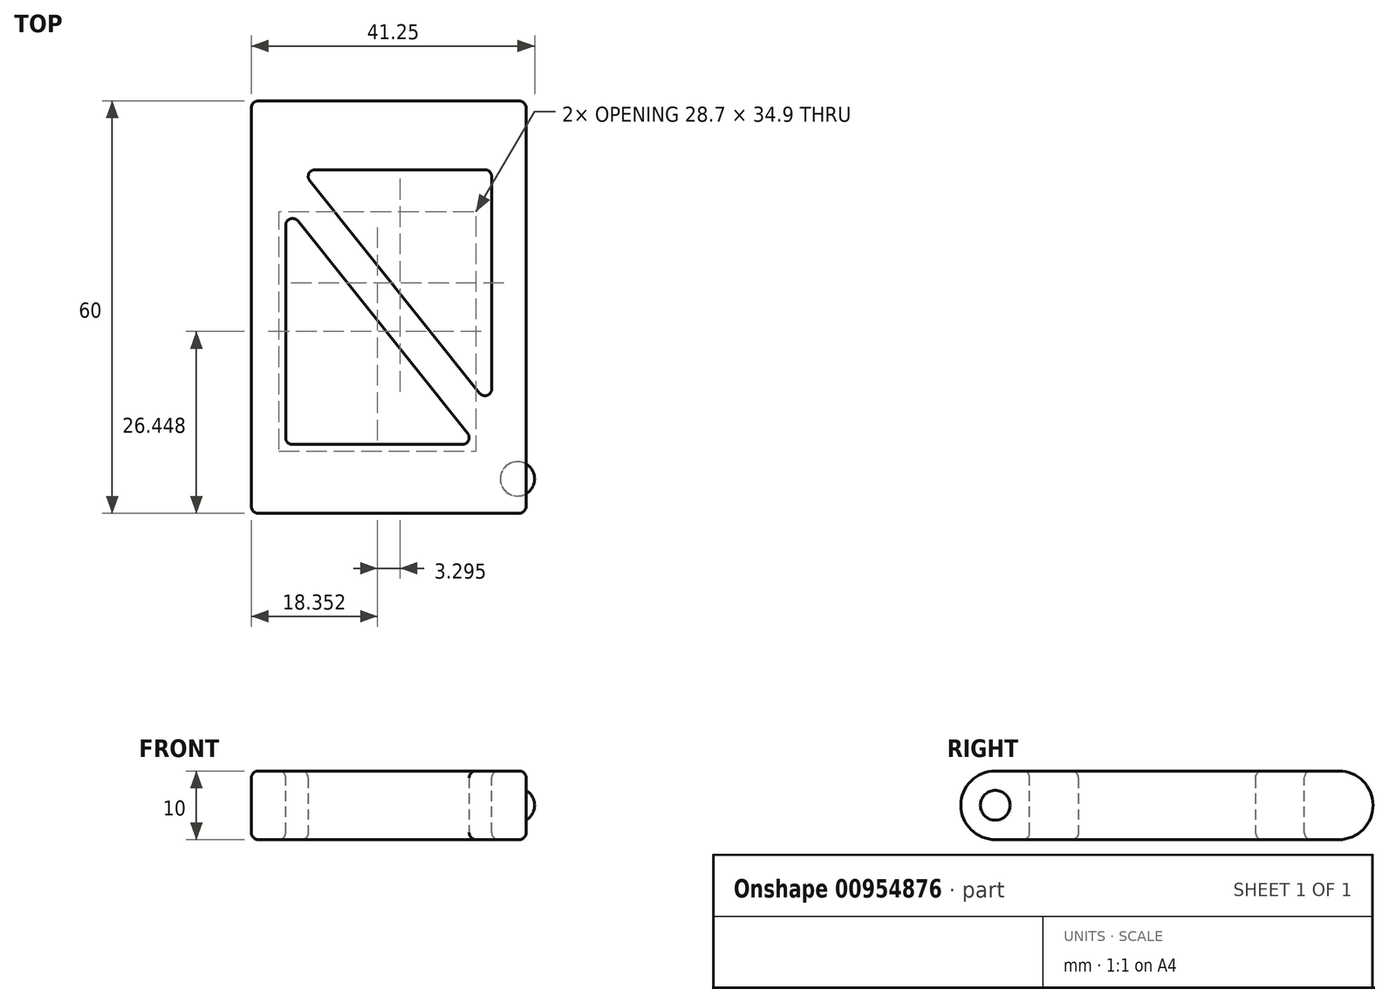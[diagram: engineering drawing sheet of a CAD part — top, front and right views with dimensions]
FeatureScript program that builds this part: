
annotation { "Feature Type Name" : "Feature", "Feature Type Description" : "" }
export const myFeature = defineFeature(function(context is Context, id is Id, definition is map)
    precondition{}
    {
        {
            var Q0;
            Q0=qCreatedBy(makeId("Top.planeOp"),FACE);
            var sketch = newSketch(context, id + "F0", { "sketchPlane" : qUnion([Q0])});
            skLineSegment(sketch, "E0.bottom", {"start": v(20, -30) * mm, "end": v(-20, -30) * mm});
            skLineSegment(sketch, "E0.top", {"start": v(20, 30) * mm, "end": v(-20, 30) * mm});
            skLineSegment(sketch, "E0.left", {"start": v(20, -30) * mm, "end": v(20, 30) * mm});
            skLineSegment(sketch, "E0.right", {"start": v(-20, -30) * mm, "end": v(-20, 30) * mm});
            skPoint(sketch, "E0.middle", {"position": v(0, 0) * mm});
            skSolve(sketch);
        }
        {
            var Q0;
            Q0=makeQuery(id+"F0.imprint","IMPRINT",FACE,{"disambiguationData":[TD([[makeQuery(id+"F0.imprint","IMPRINT",EDGE,{"derivedFrom":sQuery(id+"F0.wireOp",EDGE,"E0.bottom")}),-1.0]])]});
            extrude(context, id + "F1", {"entities" : qUnion([Q0]), "depth" : 5 * mm, "offsetDistance" : 25 * mm, "hasSecondDirection" : true, "secondDirectionOppositeDirection" : true, "secondDirectionDepth" : 5 * mm});
        }
        {
            var Q0;
            Q0=makeQuery(id+"F1.opExtrude","CAP_EDGE",EDGE,{"disambiguationData":[OSD([sQuery(id+"F0.wireOp",EDGE,"E0.bottom")])],"isStart":false});
            var Q1;
            Q1=makeQuery(id+"F1.opExtrude","CAP_EDGE",EDGE,{"disambiguationData":[OSD([sQuery(id+"F0.wireOp",EDGE,"E0.bottom")])],"isStart":true});
            var Q2;
            Q2=makeQuery(id+"F1.opExtrude","CAP_EDGE",EDGE,{"disambiguationData":[OSD([sQuery(id+"F0.wireOp",EDGE,"E0.top")])],"isStart":false});
            var Q3;
            Q3=makeQuery(id+"F1.opExtrude","CAP_EDGE",EDGE,{"disambiguationData":[OSD([sQuery(id+"F0.wireOp",EDGE,"E0.top")])],"isStart":true});
            fillet(context, id + "F2", {"entities" : qUnion([Q0, Q1, Q2, Q3]), "radius" : 5 * mm, "tangentPropagation" : true, "allowEdgeOverflow" : false});
        }
        {
            var Q0;
            Q0=qCreatedBy(makeId("Front.planeOp"),FACE);
            var Q1;
            {var subQ0=sQuery(id+"F0.wireOp",EDGE,"E0.left");var subQ1=sQuery(id+"F0.wireOp",EDGE,"E0.bottom");Q1=makeQuery(id+"F2.opFillet","BLEND_VERTEX",VERTEX,{"blendedFrom":[makeQuery(id+"F1.opExtrude","CAP_EDGE",EDGE,{"disambiguationData":[OSD([subQ1])],"isStart":false}),makeQuery(id+"F1.opExtrude","CAP_FACE",FACE,{"disambiguationData":[OSD([subQ1,sQuery(id+"F0.wireOp",EDGE,"E0.top"),subQ0,sQuery(id+"F0.wireOp",EDGE,"E0.right")])],"isStart":false}),makeQuery(id+"F1.opExtrude","SWEPT_FACE",FACE,{"disambiguationData":[OSD([subQ0])]})],"blendedInto":[makeQuery(id+"F1.opExtrude","CAP_FACE",FACE,{"disambiguationData":[OSD([subQ1,sQuery(id+"F0.wireOp",EDGE,"E0.top"),subQ0,sQuery(id+"F0.wireOp",EDGE,"E0.right")])],"isStart":false}),makeQuery(id+"F1.opExtrude","SWEPT_FACE",FACE,{"disambiguationData":[OSD([subQ0])]})]});}
            cPlane(context, id + "F3", {"entities" : qUnion([Q0, Q1]), "cplaneType" : CPlaneType.PLANE_POINT, "offset" : 25 * mm, "width" : 150 * mm, "height" : 150 * mm});
        }
        {
            var Q0;
            Q0=qCreatedBy(id+"F3.planeOp",FACE);
            var sketch = newSketch(context, id + "F4", { "sketchPlane" : qUnion([Q0])});
            skArc(sketch, "E1", {"start": v(18.75, -2.5) * mm, "mid": v(21.25, 0) * mm, "end": v(18.75, 2.5) * mm});
            skLineSegment(sketch, "E2", {"start": v(18.75, 2.5) * mm, "end": v(18.75, -2.5) * mm});
            skSolve(sketch);
        }
        {
            var Q0;
            Q0=makeQuery(id+"F4.imprint","IMPRINT",FACE,{"disambiguationData":[TD([[makeQuery(id+"F4.imprint","IMPRINT",EDGE,{"derivedFrom":sQuery(id+"F4.wireOp",EDGE,"E1")}),1.0]])]});
            var Q1;
            Q1=sQuery(id+"F4.wireOp",EDGE,"E2");
            revolve(context, id + "F5", {"operationType" : NewBodyOperationType.ADD, "surfaceOperationType" : NewSurfaceOperationType.NEW, "entities" : qUnion([Q0]), "axis" : qUnion([Q1]), "revolveType" : RevolveType.FULL});
        }
        {
            var Q0;
            Q0=qCreatedBy(makeId("Top.planeOp"),FACE);
            var sketch = newSketch(context, id + "F6", { "sketchPlane" : qUnion([Q0])});
            skLineSegment(sketch, "E3", {"start": v(-15, -20) * mm, "end": v(12.8, -20) * mm});
            skLineSegment(sketch, "E4", {"start": v(12.8, -20) * mm, "end": v(-15, 14.75) * mm});
            skLineSegment(sketch, "E5", {"start": v(-12.8, 20) * mm, "end": v(15, 20) * mm});
            skLineSegment(sketch, "E6", {"start": v(15, -14.75) * mm, "end": v(-12.8, 20) * mm});
            skLineSegment(sketch, "E7", {"start": v(-20, 25) * mm, "end": v(20, -25) * mm, "construction": true});
            skLineSegment(sketch, "E8", {"start": v(15, 20) * mm, "end": v(15, -14.75) * mm});
            skLineSegment(sketch, "E9", {"start": v(-15, 14.75) * mm, "end": v(-15, -20) * mm});
            skSolve(sketch);
        }
        {
            var Q0;
            Q0 = qSketchRegion(id + "F6", true);
            extrude(context, id + "F7", {"entities" : qUnion([Q0]), "operationType" : NewBodyOperationType.REMOVE, "endBound" : BoundingType.THROUGH_ALL, "oppositeDirection" : true, "depth" : 25 * mm, "offsetDistance" : 25 * mm, "hasSecondDirection" : true, "secondDirectionBound" : SecondDirectionBoundingType.THROUGH_ALL, "secondDirectionOppositeDirection" : false, "secondDirectionDepth" : 25 * mm});
        }
        {
            var Q0;
            Q0=makeQuery(id+"F1.opExtrude","CAP_EDGE",EDGE,{"disambiguationData":[OSD([sQuery(id+"F0.wireOp",EDGE,"E0.left")])],"isStart":false});
            var Q1;
            Q1=makeQuery(id+"F2.opFillet","BLEND_EDGE",EDGE,{"blendedFrom":[makeQuery(id+"F1.opExtrude","CAP_EDGE",EDGE,{"disambiguationData":[OSD([sQuery(id+"F0.wireOp",EDGE,"E0.top")])],"isStart":true}),makeQuery(id+"F1.opExtrude","SWEPT_FACE",FACE,{"disambiguationData":[OSD([sQuery(id+"F0.wireOp",EDGE,"E0.left")])]})],"blendedInto":[makeQuery(id+"F1.opExtrude","SWEPT_FACE",FACE,{"disambiguationData":[OSD([sQuery(id+"F0.wireOp",EDGE,"E0.left")])]})]});
            var Q2;
            Q2=makeQuery(id+"F2.opFillet","BLEND_EDGE",EDGE,{"blendedFrom":[makeQuery(id+"F1.opExtrude","CAP_EDGE",EDGE,{"disambiguationData":[OSD([sQuery(id+"F0.wireOp",EDGE,"E0.bottom")])],"isStart":true}),makeQuery(id+"F1.opExtrude","SWEPT_FACE",FACE,{"disambiguationData":[OSD([sQuery(id+"F0.wireOp",EDGE,"E0.left")])]})],"blendedInto":[makeQuery(id+"F1.opExtrude","SWEPT_FACE",FACE,{"disambiguationData":[OSD([sQuery(id+"F0.wireOp",EDGE,"E0.left")])]})]});
            var Q3;
            Q3=makeQuery(id+"F1.opExtrude","CAP_EDGE",EDGE,{"disambiguationData":[OSD([sQuery(id+"F0.wireOp",EDGE,"E0.left")])],"isStart":true});
            var Q4;
            Q4=makeQuery(id+"F1.opExtrude","CAP_EDGE",EDGE,{"disambiguationData":[OSD([sQuery(id+"F0.wireOp",EDGE,"E0.right")])],"isStart":false});
            var Q5;
            Q5=makeQuery(id+"F7.boolean.opBoolean","COPY",FACE,{"derivedFrom":makeQuery(id+"F7.opExtrude","SWEPT_FACE",FACE,{"disambiguationData":[OSD([sQuery(id+"F6.wireOp",EDGE,"E4")])]})});
            var Q6;
            Q6=makeQuery(id+"F7.boolean.opBoolean","COPY",FACE,{"derivedFrom":makeQuery(id+"F7.opExtrude","SWEPT_FACE",FACE,{"disambiguationData":[OSD([sQuery(id+"F6.wireOp",EDGE,"E3")])]})});
            var Q7;
            Q7=makeQuery(id+"F7.boolean.opBoolean","COPY",FACE,{"derivedFrom":makeQuery(id+"F7.opExtrude","SWEPT_FACE",FACE,{"disambiguationData":[OSD([sQuery(id+"F6.wireOp",EDGE,"E9")])]})});
            var Q8;
            Q8=makeQuery(id+"F7.boolean.opBoolean","COPY",FACE,{"derivedFrom":makeQuery(id+"F7.opExtrude","SWEPT_FACE",FACE,{"disambiguationData":[OSD([sQuery(id+"F6.wireOp",EDGE,"E5")])]})});
            var Q9;
            Q9=makeQuery(id+"F7.boolean.opBoolean","COPY",FACE,{"derivedFrom":makeQuery(id+"F7.opExtrude","SWEPT_FACE",FACE,{"disambiguationData":[OSD([sQuery(id+"F6.wireOp",EDGE,"E8")])]})});
            var Q10;
            Q10=makeQuery(id+"F7.boolean.opBoolean","COPY",FACE,{"derivedFrom":makeQuery(id+"F7.opExtrude","SWEPT_FACE",FACE,{"disambiguationData":[OSD([sQuery(id+"F6.wireOp",EDGE,"E6")])]})});
            fillet(context, id + "F8", {"entities" : qUnion([Q0, Q1, Q2, Q3, Q4, Q5, Q6, Q7, Q8, Q9, Q10]), "radius" : 1 * mm, "tangentPropagation" : true, "allowEdgeOverflow" : false});
        }
    });
